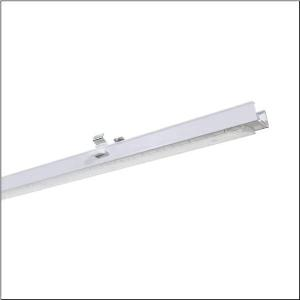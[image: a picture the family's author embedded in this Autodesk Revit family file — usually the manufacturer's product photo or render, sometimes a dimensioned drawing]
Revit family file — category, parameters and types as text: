
# Revit family: trunking_flex_31_51re12mb18b
name_source: partatom
category: Lighting Fixtures
units: mm (PartAtom-declared; Revit-internal decimal feet)

## family parameters
Cut with Voids When Loaded = No
Host = Face
Light Source = No
Part Type = Normal
Room Calculation Point = No
Round Connector Dimension = Use Diameter
Shared = No

## types (1)
- --- (1 x LED, 8000 lm, 50 W, 3500K)
    Apparent Load = 50 VA
    CIE Flux Codes = 65 91 98 99 100
    Color Rendering = 80
    Color Temperature = 3500K
    Default Elevation = 1800 mm
    Description = Trunking Flex 31, luminaire insert, of extruded aluminium section, coated, traffic white (RAL 9016), length: 1.472mm, width: 91mm, height: 53mm, LED rated luminous flux: 8.000lm, light colour: 835, control gear: ON/OFF Multilumen, with system connector: socket, mains connection: 220..240V, AC, 50/60Hz, rated input power: 50W, luminous flux adjustable on luminaire in four steps (4130/5610/6850/8000lm), connected load according to luminous flux setting (25/34/42/50W), primary light control with lens, of plastic, primary optical cover: cover, of PMMA, light emission: direct distribution, protection rating (complete): IP20, insulation class (complete): insulation class I (protective earthing), certification: CE, UKCA, impact resistance: IK02, permissible ambient temperature for indoor applications: -20..+40°C, packaging unit: 1 piece
    Height = 58 mm
    Lamp = 1 x LED
    Lamp Light Flux = 8000 lm
    Lamp Power = 50 W
    Lamp count = 1
    Length = 1472 mm
    Luminous efficacy = 160 lm/W
    Manufacturer = Siteco
    ModVariant = No
    Model = 51RE12MB18B
    Mounting Place = Ceiling
    Mounting Type = Pendant
    Number of Poles = 1
    OnlyDefault = Yes
    Power Factor = 1
    Product Name = Trunking Flex 31
    Product group = luminaire insert
    ProductGroupID = 901
    Protection Class = Protection class I
    Protection Degree = IP 20
    RLX_Detail_Level = 1
    RLX_Emergency_Light_Flux = 0 lm
    RLX_Emergency_Type = 0
    RLX_Emergency_Type_DB = No
    RlxData = <blob elided: 20325 chars, md5=33d6e987>
    Socket = socket
    Standby Power = 0 W
    System Light Flux = 8000 lm
    System Power = 50 W
    Type Comments = factory setting: luminous flux: 100 % | (ON | ON) | 300 mA
    Type Image = l_1266702.jpg
    URL = http://relux.com
    VarID = @adj_018665
    Voltage = 0 V
    Weight = 0.00 kg
    Width = 65 mm

## geometry (parser evidence)
native form markers: Blend x4, Sweep x10
no freeform markers — native parametric forms only
